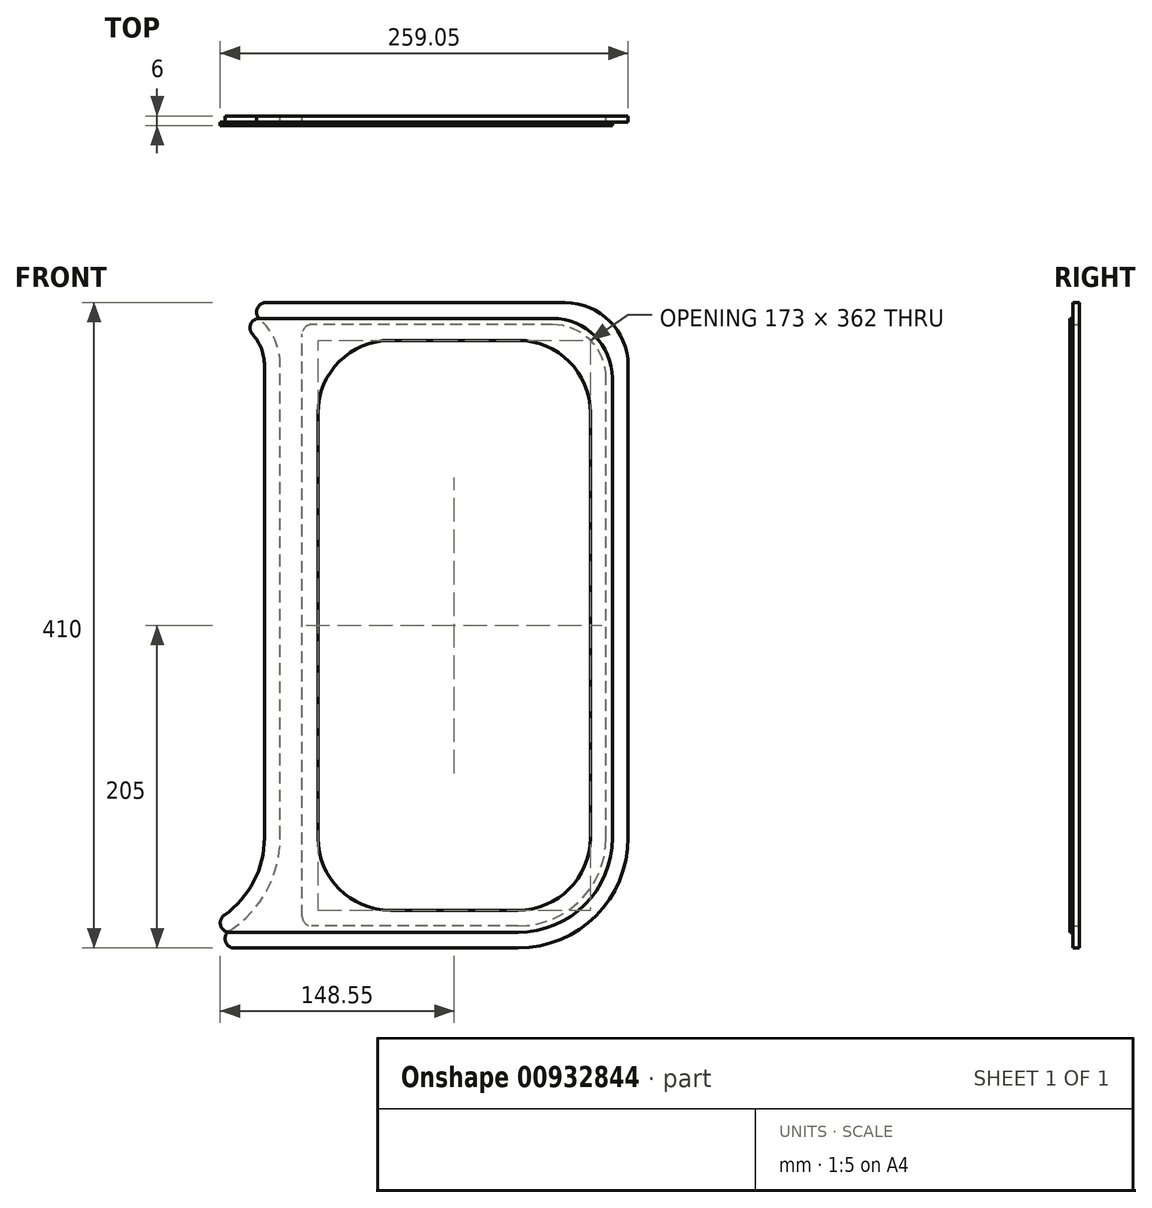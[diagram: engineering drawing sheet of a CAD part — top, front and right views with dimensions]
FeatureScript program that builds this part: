
annotation { "Feature Type Name" : "Feature", "Feature Type Description" : "" }
export const myFeature = defineFeature(function(context is Context, id is Id, definition is map)
    precondition{}
    {
        {
            var Q0;
            Q0=qCreatedBy(makeId("Front.planeOp"),FACE);
            var sketch = newSketch(context, id + "F0", { "sketchPlane" : qUnion([Q0])});
            skLineSegment(sketch, "E0.bottom", {"start": v(40.5, -205) * mm, "end": v(-110.5, -205) * mm});
            skLineSegment(sketch, "E0.top", {"start": v(70.5, 205) * mm, "end": v(-110.5, 205) * mm});
            skLineSegment(sketch, "E0.left", {"start": v(110.5, -135) * mm, "end": v(110.5, 165) * mm});
            skLineSegment(sketch, "E0.right", {"start": v(-110.5, -135) * mm, "end": v(-110.5, 165) * mm});
            skPoint(sketch, "E0.middle", {"position": v(0, 0) * mm});
            skPoint(sketch, "E1.visualSharp", {"position": v(110.5, 205) * mm});
            skArc(sketch, "E1.filletArc", {"start": v(110.5, 165) * mm, "mid": v(98.78, 193.28) * mm, "end": v(70.5, 205) * mm});
            skPoint(sketch, "E2.visualSharp", {"position": v(110.5, -205) * mm});
            skArc(sketch, "E2.filletArc", {"start": v(40.5, -205) * mm, "mid": v(90, -184.5) * mm, "end": v(110.5, -135) * mm});
            skLineSegment(sketch, "E3", {"start": v(-110.5, 205) * mm, "end": v(-119.52, 205) * mm});
            skLineSegment(sketch, "E4", {"start": v(-110.5, -205) * mm, "end": v(-139.51, -205) * mm});
            skArc(sketch, "E5", {"start": v(-110.5, 165) * mm, "mid": v(-113.9, 181.16) * mm, "end": v(-123.56, 194.57) * mm});
            skArc(sketch, "E6", {"start": v(-142.75, -193.95) * mm, "mid": v(-119.09, -168.6) * mm, "end": v(-110.5, -135) * mm});
            skPoint(sketch, "E7.visualSharp", {"position": v(-150.5, 205) * mm});
            skArc(sketch, "E7.filletArc", {"start": v(-119.52, 205) * mm, "mid": v(-125.11, 201.17) * mm, "end": v(-123.56, 194.57) * mm});
            skPoint(sketch, "E8.visualSharp", {"position": v(-180.5, -205) * mm});
            skArc(sketch, "E8.filletArc", {"start": v(-142.75, -193.95) * mm, "mid": v(-145.27, -200.69) * mm, "end": v(-139.51, -205) * mm});
            skArc(sketch, "E9.0", {"start": v(40.5, -195) * mm, "mid": v(82.93, -177.43) * mm, "end": v(100.5, -135) * mm});
            skLineSegment(sketch, "E9.3", {"start": v(62.5, 195) * mm, "end": v(-100.5, 195) * mm});
            skLineSegment(sketch, "E9.6", {"start": v(100.5, -135) * mm, "end": v(100.5, 157) * mm});
            skLineSegment(sketch, "E9.7", {"start": v(-100.5, -195) * mm, "end": v(-100.5, 195) * mm});
            skLineSegment(sketch, "E9.11", {"start": v(40.5, -195) * mm, "end": v(-40.5, -195) * mm});
            skArc(sketch, "E10.0", {"start": v(-120.5, 165) * mm, "mid": v(-122.47, 175.7) * mm, "end": v(-128.14, 185) * mm});
            skLineSegment(sketch, "E10.1", {"start": v(-120.5, -135) * mm, "end": v(-120.5, 165) * mm});
            skArc(sketch, "E10.2", {"start": v(-146, -184.1) * mm, "mid": v(-127.26, -162.66) * mm, "end": v(-120.5, -135) * mm});
            skArc(sketch, "E11.filletArc", {"start": v(-146, -184.1) * mm, "mid": v(-148.27, -190.8) * mm, "end": v(-142.55, -195) * mm});
            skPoint(sketch, "E12.visualSharp", {"position": v(-150.5, 195) * mm});
            skArc(sketch, "E12.filletArc", {"start": v(-123.67, 195) * mm, "mid": v(-129.14, 191.45) * mm, "end": v(-128.14, 185) * mm});
            skPoint(sketch, "E13.visualSharp", {"position": v(-105.67, -183) * mm});
            skPoint(sketch, "E14.visualSharp", {"position": v(-88.5, 183) * mm});
            skPoint(sketch, "E15.visualSharp", {"position": v(88.5, 183) * mm});
            skPoint(sketch, "E16.visualSharp", {"position": v(-100.5, -195) * mm});
            skLineSegment(sketch, "E17.1", {"start": v(96.5, -135) * mm, "end": v(96.5, 157) * mm});
            skLineSegment(sketch, "E17.2", {"start": v(-96.5, -185) * mm, "end": v(-96.5, 185) * mm});
            skLineSegment(sketch, "E17.4", {"start": v(40.5, -191) * mm, "end": v(-90.5, -191) * mm});
            skLineSegment(sketch, "E17.5", {"start": v(62.5, 191) * mm, "end": v(-90.5, 191) * mm});
            skArc(sketch, "E17.6", {"start": v(40.5, -191) * mm, "mid": v(80.1, -174.6) * mm, "end": v(96.5, -135) * mm});
            skLineSegment(sketch, "E18.1", {"start": v(86.5, -135) * mm, "end": v(86.5, 135) * mm});
            skLineSegment(sketch, "E18.2", {"start": v(-86.5, -135) * mm, "end": v(-86.5, 135) * mm});
            skArc(sketch, "E18.3", {"start": v(-86.5, -135) * mm, "mid": v(-73.03, -167.53) * mm, "end": v(-40.5, -181) * mm});
            skLineSegment(sketch, "E18.4", {"start": v(40.5, -181) * mm, "end": v(-40.5, -181) * mm});
            skLineSegment(sketch, "E18.5", {"start": v(40.5, 181) * mm, "end": v(-40.5, 181) * mm});
            skArc(sketch, "E18.6", {"start": v(40.5, -181) * mm, "mid": v(73.03, -167.53) * mm, "end": v(86.5, -135) * mm});
            skArc(sketch, "E19.filletArc", {"start": v(86.5, 135) * mm, "mid": v(73.03, 167.53) * mm, "end": v(40.5, 181) * mm});
            skPoint(sketch, "E20.visualSharp", {"position": v(-86.5, 181) * mm});
            skArc(sketch, "E20.filletArc", {"start": v(-40.5, 181) * mm, "mid": v(-73.03, 167.53) * mm, "end": v(-86.5, 135) * mm});
            skLineSegment(sketch, "E21", {"start": v(-100.5, 195) * mm, "end": v(-123.67, 195) * mm});
            skLineSegment(sketch, "E22", {"start": v(-40.5, -195) * mm, "end": v(-142.55, -195) * mm});
            skPoint(sketch, "E23.visualSharp", {"position": v(100.5, 195) * mm});
            skArc(sketch, "E23.filletArc", {"start": v(100.5, 157) * mm, "mid": v(89.37, 183.87) * mm, "end": v(62.5, 195) * mm});
            skArc(sketch, "E24.0", {"start": v(96.5, 157) * mm, "mid": v(86.54, 181.04) * mm, "end": v(62.5, 191) * mm});
            skPoint(sketch, "E25.visualSharp", {"position": v(-96.5, 191) * mm});
            skArc(sketch, "E25.filletArc", {"start": v(-90.5, 191) * mm, "mid": v(-94.74, 189.24) * mm, "end": v(-96.5, 185) * mm});
            skPoint(sketch, "E26.visualSharp", {"position": v(-96.5, -191) * mm});
            skArc(sketch, "E26.filletArc", {"start": v(-96.5, -185) * mm, "mid": v(-94.74, -189.24) * mm, "end": v(-90.5, -191) * mm});
            skSolve(sketch);
        }
        {
            var Q0;
            Q0=makeQuery(id+"F0.imprint","IMPRINT",FACE,{"disambiguationData":[TD([[makeQuery(id+"F0.imprint","IMPRINT",EDGE,{"derivedFrom":sQuery(id+"F0.wireOp",EDGE,"E9.0")}),1.0]])]});
            var Q1;
            Q1=makeQuery(id+"F0.imprint","IMPRINT",FACE,{"disambiguationData":[TD([[makeQuery(id+"F0.imprint","IMPRINT",EDGE,{"derivedFrom":sQuery(id+"F0.wireOp",EDGE,"E0.right")}),-1.0]])]});
            var Q2;
            Q2=makeQuery(id+"F0.imprint","IMPRINT",FACE,{"disambiguationData":[TD([[makeQuery(id+"F0.imprint","IMPRINT",EDGE,{"derivedFrom":sQuery(id+"F0.wireOp",EDGE,"E0.right")}),1.0]])]});
            var Q3;
            Q3=makeQuery(id+"F0.imprint","IMPRINT",FACE,{"disambiguationData":[TD([[makeQuery(id+"F0.imprint","IMPRINT",EDGE,{"derivedFrom":sQuery(id+"F0.wireOp",EDGE,"fd6b8477-feee-4e7d-ba72-d92cecb9d04f.0")}),-1.0]])]});
            var Q4;
            {var subQ3=sQuery(id+"F0.wireOp",EDGE,"178d0af1-d49c-41d6-87ab-4619a4af833a.0");Q4=makeQuery(id+"F0.imprint","IMPRINT",FACE,{"disambiguationData":[TD([[makeQuery(id+"F0.imprint","IMPRINT",EDGE,{"derivedFrom":subQ3}),-1.0]])]});}
            var Q5;
            Q5=makeQuery(id+"F0.imprint","IMPRINT",FACE,{"disambiguationData":[TD([[makeQuery(id+"F0.imprint","IMPRINT",EDGE,{"derivedFrom":sQuery(id+"F0.wireOp",EDGE,"E17.1")}),1.0]])]});
            extrude(context, id + "F1", {"entities" : qUnion([Q0, Q1, Q2, Q3, Q4, Q5]), "depth" : 6 * mm, "offsetDistance" : 25 * mm});
        }
        {
            var Q0;
            Q0=makeQuery(id+"F0.imprint","IMPRINT",FACE,{"disambiguationData":[TD([[makeQuery(id+"F0.imprint","IMPRINT",EDGE,{"derivedFrom":sQuery(id+"F0.wireOp",EDGE,"E0.bottom")}),-1.0]])]});
            extrude(context, id + "F2", {"entities" : qUnion([Q0]), "operationType" : NewBodyOperationType.ADD, "depth" : 4 * mm, "offsetDistance" : 25 * mm});
        }
        {
            var Q0;
            Q0=makeQuery(id+"F0.imprint","IMPRINT",FACE,{"disambiguationData":[TD([[makeQuery(id+"F0.imprint","IMPRINT",EDGE,{"derivedFrom":sQuery(id+"F0.wireOp",EDGE,"E0.right")}),1.0]])]});
            extrude(context, id + "F3", {"entities" : qUnion([Q0]), "operationType" : NewBodyOperationType.REMOVE, "depth" : 4 * mm, "offsetDistance" : 25 * mm});
        }
        {
            var Q0;
            Q0=makeQuery(id+"F0.imprint","IMPRINT",FACE,{"disambiguationData":[TD([[makeQuery(id+"F0.imprint","IMPRINT",EDGE,{"derivedFrom":sQuery(id+"F0.wireOp",EDGE,"E17.1")}),1.0]])]});
            extrude(context, id + "F4", {"entities" : qUnion([Q0]), "operationType" : NewBodyOperationType.REMOVE, "depth" : 4 * mm, "offsetDistance" : 25 * mm});
        }
    });
